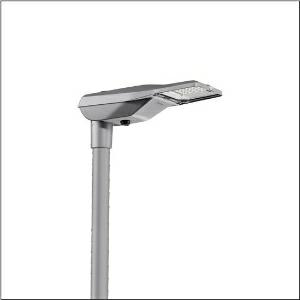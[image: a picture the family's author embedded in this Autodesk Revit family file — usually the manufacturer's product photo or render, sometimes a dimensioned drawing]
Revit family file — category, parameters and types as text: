
# Revit family: streetlight_sl_21_iq_micro___st1_0a_5xe1d31u08cb_b584
name_source: partatom
category: Lighting Fixtures
units: mm (PartAtom-declared; Revit-internal decimal feet)

## family parameters
Cut with Voids When Loaded = No
Host = Face
Light Source = No
Part Type = Normal
Room Calculation Point = No
Round Connector Dimension = Use Diameter
Shared = No

## types (1)
- --- (1 x LED, 2880 lm, 19.1 W, 3000K)
    Apparent Load = 19 VA
    CIE Flux Codes = 37 72 97 100 100
    Color Rendering = 70
    Color Temperature = 3000K
    Default Elevation = 1800 mm
    Description = Streetlight SL 21 iQ micro, mast luminaire, primary light control with lens, of PMMA, primary optical cover: cover, of toughened safety glass, transparent, light distribution: ST1.0a, light emission: direct distribution, primary light characteristic: asymmetric, installation type: post-top, side-entry, LED, High Power LED, rated luminous flux: 2.880lm, luminous efficacy: 151lm/W, light colour: 730, colour temperature: 3000K, control gear: iQ-Street Remote, D4i with power reduction, control: pre-setting: logarithmic dimming characteristic, Street-Remote, Auto-Match, Temp-Guard, Lumen-Switch, Night-Set, Smart-Wire, Light-Fading, Desk-Remote (wireless, voltage-free reading and setting of iQ features in the workshop via application-optimized NFC function/RFID function), optimised constant luminous flux control (CLO 2.0), mains connection: 220..240V, AC, 50/60Hz, start of lifetime: 19W, end of service life: 20W, reduction: 9W, luminaire housing, of diecast aluminium, powder-coated, Siteco® metallic grey (DB 702S), corrosivity category C5 mid according to DIN EN ISO 12944, please order mast flange separately, inclination adjustable: 0°, 5°, 10°, 15°, sealing non-destructively replaceable, multi-level sealing system, length: 528mm, width: 235mm, height: 110mm, mast flange for spigot size: 42mm (side-entry): 5XC10008XM4, 60/48mm (side-entry/post-top): 5XC10108XM2, 76/60mm (side-entry/post-top): 5XC10108XM1, mounting height: 4..8m, Smart Interface below, protection rating (complete): IP66, insulation class (complete): insulation class II (safety insulation), certification: CE, ENEC, ENEC+, VDE, impact resistance: IK10, permissible operating ambient temperature for outdoor applications: -40..+50°C, standard-compliant lighting for roads and squares, packaging unit: 1 piece

Light Distribution: ST1.0a
    Height = 110 mm
    Lamp = 1 x LED
    Lamp Light Flux = 2880 lm
    Lamp Power = 19.1 W
    Lamp count = 1
    Length = 528 mm
    Luminous efficacy = 151 lm/W
    Manufacturer = Siteco
    ModVariant = No
    Model = 5XE1D31U08CB
    Number of Poles = 1
    OnlyDefault = Yes
    Power Factor = 1
    Product Name = Streetlight SL 21 iQ micro | ST1.0a
    Product group = mast luminaire | pylon top
    ProductGroupID = 6100
    Protection Class = Protection class II
    Protection Degree = IP 66
    RLX_Detail_Level = 1
    RLX_Emergency_Light_Flux = 0 lm
    RLX_Emergency_Type = 0
    RLX_Emergency_Type_DB = No
    RlxData = <blob elided: 99213 chars, md5=cedfded6>
    Socket = socket
    Standby Power = 0 W
    System Light Flux = 2880 lm
    System Power = 19 W
    Type Comments = factory setting: luminous flux: 100 % | dim-lin: 254 | 387 mA
    Type Image = l_1277290.jpg
    URL = http://relux.com
    VarID = @adj_115760
    Voltage = 0 V
    Weight = 0.00 kg
    Width = 235 mm

## geometry (parser evidence)
native form markers: Blend x4, Sweep x10
no freeform markers — native parametric forms only
